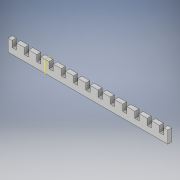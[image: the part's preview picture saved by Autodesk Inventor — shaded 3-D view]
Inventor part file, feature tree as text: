
AUTODESK INVENTOR PART (.ipt)
format: ipt  version: 2017 (Build 210142000, 142)  size: 165,376 bytes
history: native  units: in
note: dims shown in document units (in); Inventor stores cm internally (conversion verified against a paired STEP export)
features: mirror x6, plane x2, extrude x1, sketch x1
ambient origin geometry x8: Origin, YZ Plane, XZ Plane, XY Plane, X Axis, Y Axis, Z Axis, Center Point
bodies: Solid1 (feature_tree)
feature tree (10):
  extrude  "Extrusion1"  Depth=0.2047in
  mirror  "Mirror1"
  mirror  "Mirror2"
  mirror  "Mirror3"
  mirror  "Mirror4"
  mirror  "Mirror5"
  plane  "Work Plane1"
  mirror  "Mirror6"
  sketch  "Sketch1"  dims[d0=0.5906in d1=0.2047in d2=0.1969in d3=0.1969in d4=0.2953in d5=0.1969in d6=0.0in]
  plane  "Work Plane2"
